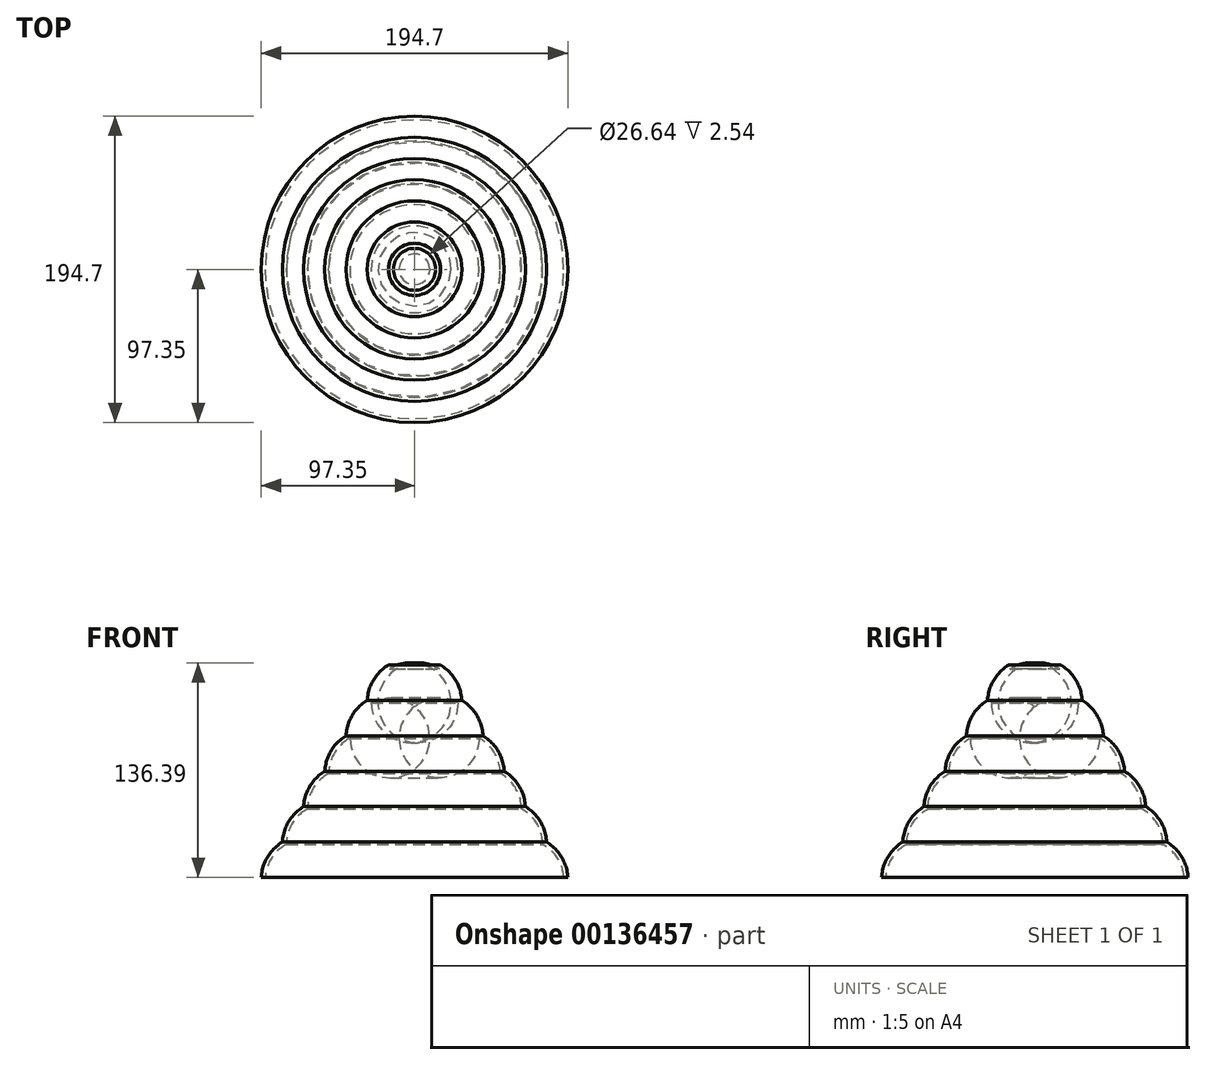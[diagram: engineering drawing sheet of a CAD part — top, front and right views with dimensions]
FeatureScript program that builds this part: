
annotation { "Feature Type Name" : "Feature", "Feature Type Description" : "" }
export const myFeature = defineFeature(function(context is Context, id is Id, definition is map)
    precondition{}
    {
        {
            var Q0;
            Q0=qCreatedBy(makeId("Front.planeOp"),FACE);
            var sketch = newSketch(context, id + "F0", { "sketchPlane" : qUnion([Q0])});
            skArc(sketch, "E0", {"start": v(-16.59, 69.28) * mm, "mid": v(-26.12, 59.71) * mm, "end": v(-30.05, 46.8) * mm});
            skArc(sketch, "E1.MirrorCS", {"start": v(-43.5, 24.31) * mm, "mid": v(-53.04, 14.75) * mm, "end": v(-56.97, 1.83) * mm});
            skArc(sketch, "E2.MirrorCS", {"start": v(-70.43, -20.65) * mm, "mid": v(-79.96, -30.22) * mm, "end": v(-83.89, -43.14) * mm});
            skLineSegment(sketch, "E3", {"start": v(-16.59, 69.28) * mm, "end": v(-97.35, -65.62) * mm, "construction": true});
            skArc(sketch, "E4.MirrorCS", {"start": v(-43.5, 24.31) * mm, "mid": v(-39.58, 37.23) * mm, "end": v(-30.05, 46.8) * mm});
            skArc(sketch, "E5.MirrorCS", {"start": v(-70.43, -20.65) * mm, "mid": v(-66.5, -7.74) * mm, "end": v(-56.97, 1.83) * mm});
            skArc(sketch, "E6.MirrorCS", {"start": v(-97.35, -65.62) * mm, "mid": v(-93.42, -52.7) * mm, "end": v(-83.89, -43.14) * mm});
            skLineSegment(sketch, "E7", {"start": v(-97.35, -65.62) * mm, "end": v(0, -65.62) * mm});
            skLineSegment(sketch, "E8", {"start": v(0, -65.62) * mm, "end": v(0, 69.28) * mm});
            skLineSegment(sketch, "E9", {"start": v(0, 69.28) * mm, "end": v(-16.59, 69.28) * mm});
            skSolve(sketch);
        }
        {
            var Q0;
            Q0=qCreatedBy(makeId("Top.planeOp"),FACE);
            cPlane(context, id + "F1", {"entities" : qUnion([Q0]), "cplaneType" : CPlaneType.OFFSET, "offset" : 254 * mm, "width" : 152.4 * mm, "height" : 152.4 * mm});
        }
        {
            var Q0;
            Q0=qCreatedBy(id+"F1.planeOp",FACE);
            var sketch = newSketch(context, id + "F2", { "sketchPlane" : qUnion([Q0])});
            skCircle(sketch, "E10", {"center": v(0, 0) * mm, "radius": 16.07 * mm});
            skSolve(sketch);
        }
        {
            var Q0;
            Q0=makeQuery(id+"F0.imprint","IMPRINT",FACE,{"disambiguationData":[TD([[makeQuery(id+"F0.imprint","IMPRINT",EDGE,{"derivedFrom":sQuery(id+"F0.wireOp",EDGE,"E0")}),1.0]])]});
            var Q1;
            Q1=sQuery(id+"F2.wireOp",EDGE,"E10");
            revolve(context, id + "F3", {"entities" : qUnion([Q0]), "axis" : qUnion([Q1]), "revolveType" : RevolveType.FULL});
        }
        {
            var Q0;
            Q0=makeQuery(id+"F3.opRevolve","SWEPT_FACE",FACE,{"disambiguationData":[OSD([sQuery(id+"F0.wireOp",EDGE,"E7")])]});
            shell(context, id + "F4", {"entities" : qUnion([Q0]), "thickness" : 2.54 * mm});
        }
        {
            var Q0;
            Q0=makeQuery(id+"F3.opRevolve","SWEPT_FACE",FACE,{"disambiguationData":[OSD([sQuery(id+"F0.wireOp",EDGE,"E9")])]});
            var sketch = newSketch(context, id + "F5", { "sketchPlane" : qUnion([Q0])});
            skCircle(sketch, "E11", {"center": v(0, 0) * mm, "radius": 13.32 * mm});
            skSolve(sketch);
        }
        {
            var Q0;
            Q0 = qSketchRegion(id + "F5", true);
            extrude(context, id + "F6", {"entities" : qUnion([Q0]), "operationType" : NewBodyOperationType.REMOVE, "oppositeDirection" : true, "depth" : 25.4 * mm});
        }
    });
